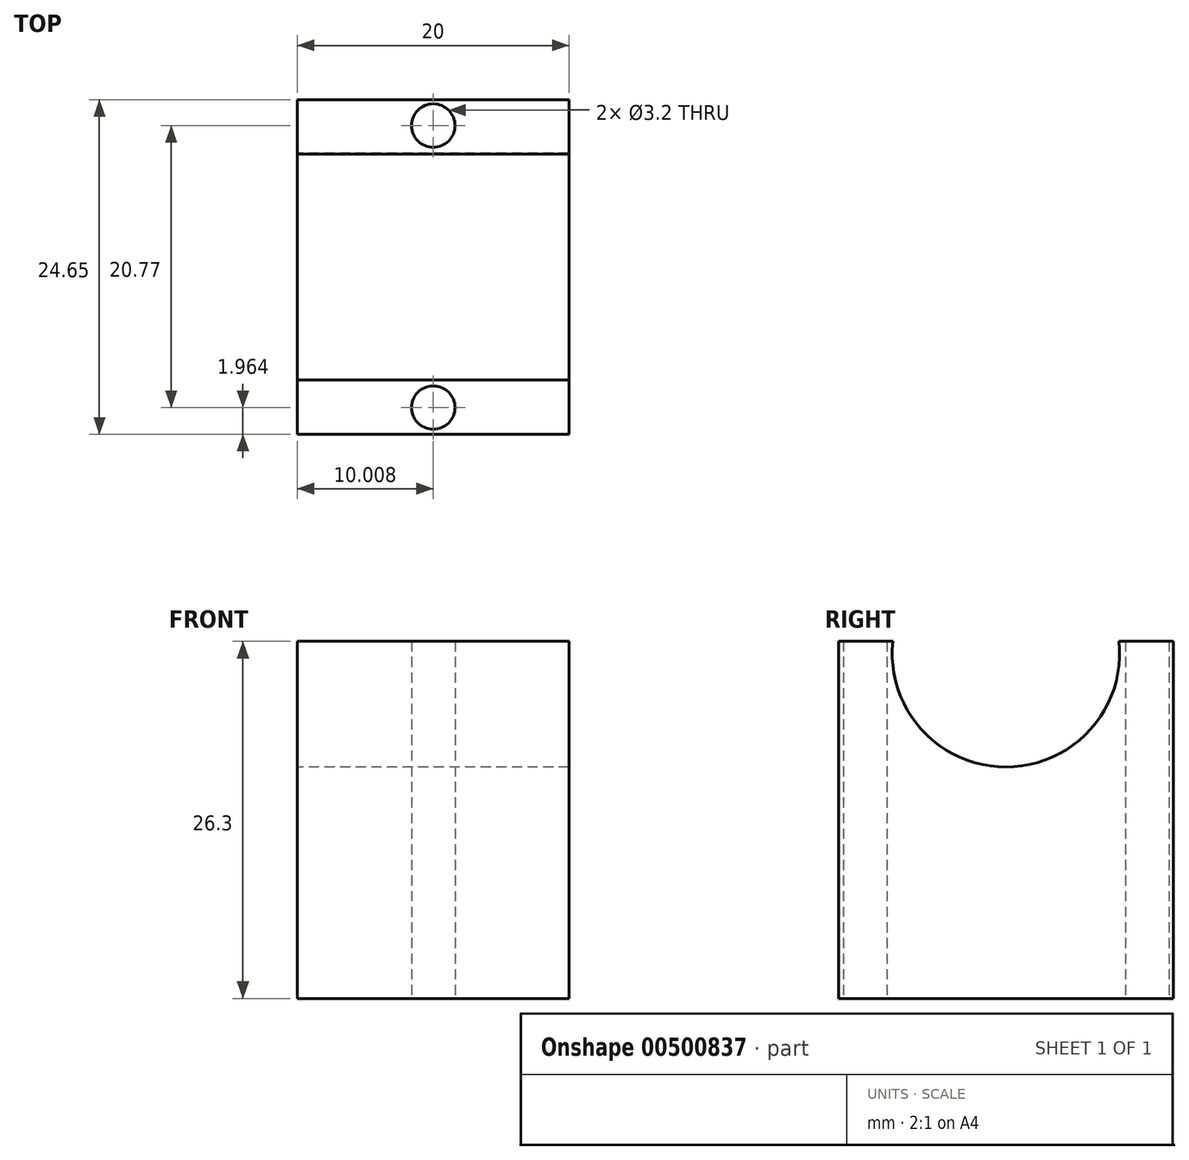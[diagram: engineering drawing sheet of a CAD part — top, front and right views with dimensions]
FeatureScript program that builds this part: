
annotation { "Feature Type Name" : "Feature", "Feature Type Description" : "" }
export const myFeature = defineFeature(function(context is Context, id is Id, definition is map)
    precondition{}
    {
        {
            var Q0;
            Q0=qCreatedBy(makeId("Right.planeOp"),FACE);
            var sketch = newSketch(context, id + "F0", { "sketchPlane" : qUnion([Q0])});
            skLineSegment(sketch, "E0", {"start": v(-7.77, 9.24) * mm, "end": v(-11.77, 9.24) * mm});
            skLineSegment(sketch, "E1", {"start": v(-11.77, 9.24) * mm, "end": v(-11.77, -17.06) * mm});
            skLineSegment(sketch, "E2", {"start": v(-11.77, -17.06) * mm, "end": v(12.88, -17.06) * mm});
            skLineSegment(sketch, "E3", {"start": v(12.88, -17.06) * mm, "end": v(12.88, 9.24) * mm});
            skLineSegment(sketch, "E4", {"start": v(12.88, 9.24) * mm, "end": v(8.88, 9.24) * mm});
            skLineSegment(sketch, "E5", {"start": v(0.55, 0.92) * mm, "end": v(0.55, -17.06) * mm});
            skPoint(sketch, "E5.startSnap0", {"position": v(0.55, -17.06) * mm});
            skPoint(sketch, "E5.endSnap0", {"position": v(0.55, 0.92) * mm});
            skArc(sketch, "E6", {"start": v(-7.77, 9.24) * mm, "mid": v(0.55, -0.02) * mm, "end": v(8.88, 9.24) * mm});
            skSolve(sketch);
        }
        {
            var Q0;
            Q0 = qSketchRegion(id + "F0", true);
            extrude(context, id + "F1", {"entities" : qUnion([Q0]), "depth" : 20 * mm, "offsetDistance" : 25 * mm});
        }
        {
            var Q0;
            Q0=qCreatedBy(makeId("Top.planeOp"),FACE);
            var sketch = newSketch(context, id + "F2", { "sketchPlane" : qUnion([Q0])});
            skLineSegment(sketch, "E7", {"start": v(10, -7.83) * mm, "end": v(10, -11.78) * mm});
            skPoint(sketch, "E8", {"position": v(10, -8.2) * mm});
            skLineSegment(sketch, "E9", {"start": v(10, 8.9) * mm, "end": v(10, 12.79) * mm});
            skPoint(sketch, "E10", {"position": v(10, 9.2) * mm});
            skCircle(sketch, "E11", {"center": v(10, 10.96) * mm, "radius": 1.6 * mm});
            skCircle(sketch, "E12", {"center": v(10, -9.8) * mm, "radius": 1.6 * mm});
            skLineSegment(sketch, "E13", {"start": v(10, 0.48) * mm, "end": v(10, -9.9) * mm});
            skLineSegment(sketch, "E14", {"start": v(10, 0.48) * mm, "end": v(10, 10.86) * mm});
            skLineSegment(sketch, "E15", {"start": v(10, 10.96) * mm, "end": v(10, -9.8) * mm});
            skLineSegment(sketch, "E16", {"start": v(0, 0) * mm, "end": v(20, 0) * mm, "construction": true});
            skLineSegment(sketch, "E17", {"start": v(10, 8.9) * mm, "end": v(10, -8.2) * mm, "construction": true});
            skSolve(sketch);
        }
        {
            var Q0;
            Q0 = qSketchRegion(id + "F2", true);
            extrude(context, id + "F3", {"entities" : qUnion([Q0]), "operationType" : NewBodyOperationType.REMOVE, "depth" : 40 * mm, "offsetDistance" : 25 * mm, "symmetric" : true});
        }
    });
